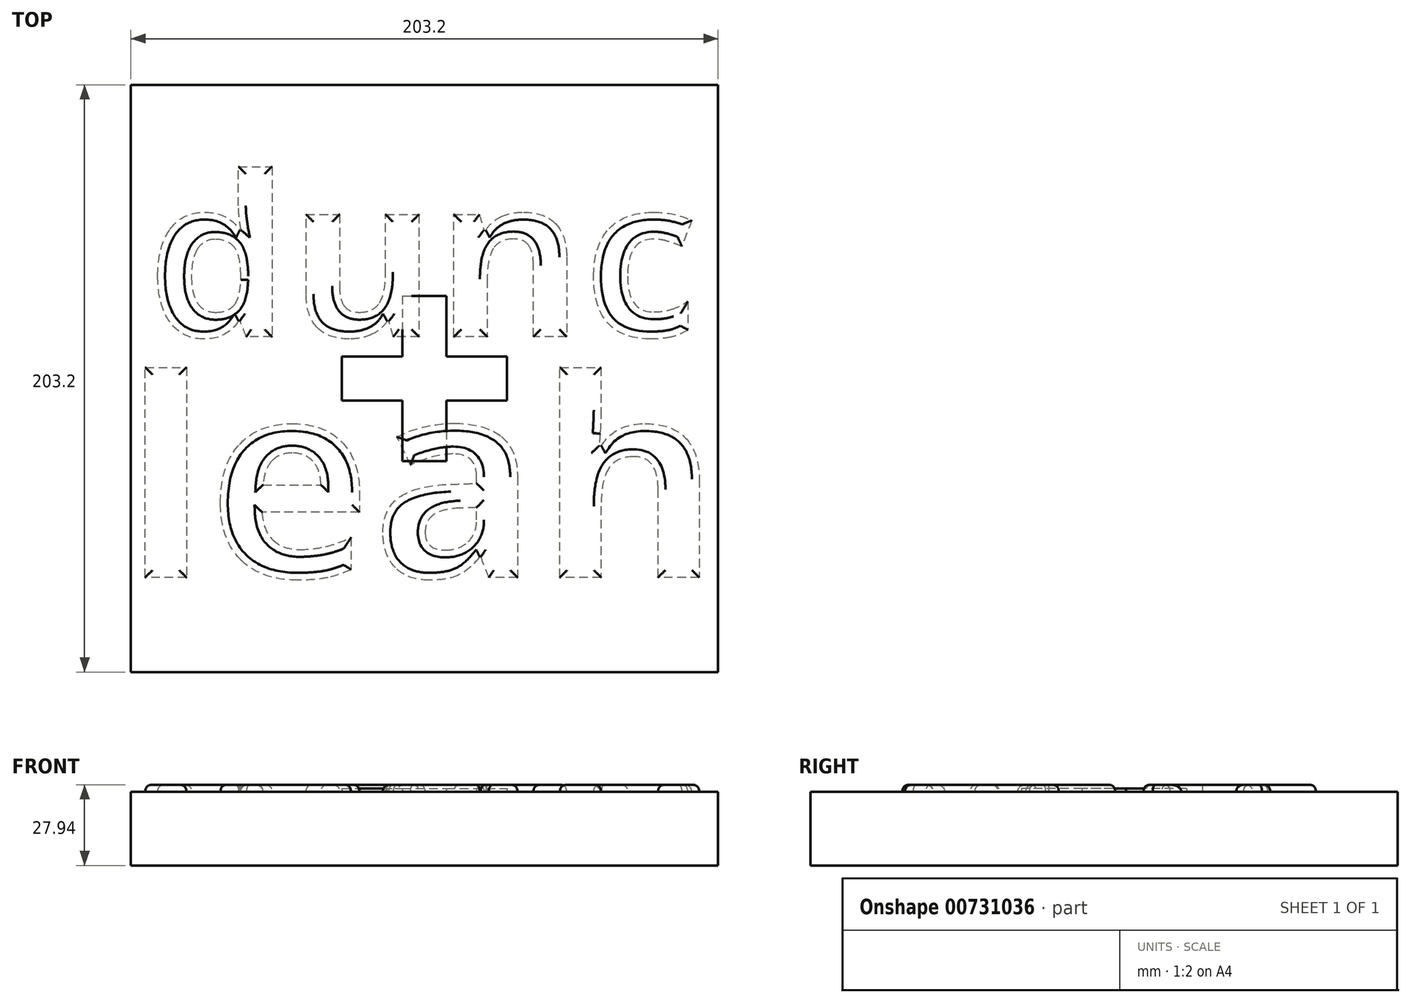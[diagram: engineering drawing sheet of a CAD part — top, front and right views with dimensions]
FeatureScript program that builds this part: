
annotation { "Feature Type Name" : "Feature", "Feature Type Description" : "" }
export const myFeature = defineFeature(function(context is Context, id is Id, definition is map)
    precondition{}
    {
        {
            var Q0;
            Q0=qCreatedBy(makeId("Top.planeOp"),FACE);
            var sketch = newSketch(context, id + "F0", { "sketchPlane" : qUnion([Q0])});
            skLineSegment(sketch, "E0.bottom", {"start": v(-101.6, 101.6) * mm, "end": v(101.6, 101.6) * mm});
            skLineSegment(sketch, "E0.top", {"start": v(-101.6, -101.6) * mm, "end": v(101.6, -101.6) * mm});
            skLineSegment(sketch, "E0.left", {"start": v(-101.6, 101.6) * mm, "end": v(-101.6, -101.6) * mm});
            skLineSegment(sketch, "E0.right", {"start": v(101.6, 101.6) * mm, "end": v(101.6, -101.6) * mm});
            skPoint(sketch, "E0.middle", {"position": v(0, 0) * mm});
            skText(sketch, "E1", { "text": "dunc", "fontName": "OpenSans-Bold.ttf"});
            skText(sketch, "E2", { "text": "leah", "fontName": "OpenSans-Bold.ttf"});
            const initialGuessF0  = {"E1": [-0.0958, 0.01441, 1, 0, 0.05578], "E2": [-0.1041, -0.06888, 1, 0, 0.06888]};
            skSetInitialGuess(sketch, initialGuessF0);
            skSolve(sketch);
        }
        {
            var Q0;
            Q0=makeQuery(id+"F0.imprint","IMPRINT",FACE,{"disambiguationData":[TD([[makeQuery(id+"F0.imprint","IMPRINT",EDGE,{"derivedFrom":sQuery(id+"F0.wireOp",EDGE,"E2.sketch_text.stroke-42")}),1.0]])]});
            var Q1;
            Q1=makeQuery(id+"F0.imprint","IMPRINT",FACE,{"disambiguationData":[TD([[makeQuery(id+"F0.imprint","IMPRINT",EDGE,{"derivedFrom":sQuery(id+"F0.wireOp",EDGE,"E1.sketch_text.stroke-14")}),1.0]])]});
            var Q2;
            Q2=makeQuery(id+"F0.imprint","IMPRINT",FACE,{"disambiguationData":[TD([[makeQuery(id+"F0.imprint","IMPRINT",EDGE,{"derivedFrom":sQuery(id+"F0.wireOp",EDGE,"E2.sketch_text.stroke-4")}),1.0]])]});
            var Q3;
            Q3=makeQuery(id+"F0.imprint","IMPRINT",FACE,{"disambiguationData":[TD([[makeQuery(id+"F0.imprint","IMPRINT",EDGE,{"derivedFrom":sQuery(id+"F0.wireOp",EDGE,"E0.bottom")}),-1.0]])]});
            var Q4;
            Q4=makeQuery(id+"F2.opExtrude","CAP_FACE",FACE,{"disambiguationData":[OSD([sQuery(id+"F0.wireOp",EDGE,"E1.sketch_text.stroke-0"),sQuery(id+"F0.wireOp",EDGE,"E1.sketch_text.stroke-1"),sQuery(id+"F0.wireOp",EDGE,"E1.sketch_text.stroke-2"),sQuery(id+"F0.wireOp",EDGE,"E1.sketch_text.stroke-3"),sQuery(id+"F0.wireOp",EDGE,"E1.sketch_text.stroke-4"),sQuery(id+"F0.wireOp",EDGE,"E1.sketch_text.stroke-5"),sQuery(id+"F0.wireOp",EDGE,"E1.sketch_text.stroke-6"),sQuery(id+"F0.wireOp",EDGE,"E1.sketch_text.stroke-7"),sQuery(id+"F0.wireOp",EDGE,"E1.sketch_text.stroke-8"),sQuery(id+"F0.wireOp",EDGE,"E1.sketch_text.stroke-9"),sQuery(id+"F0.wireOp",EDGE,"E1.sketch_text.stroke-10"),sQuery(id+"F0.wireOp",EDGE,"E1.sketch_text.stroke-11"),sQuery(id+"F0.wireOp",EDGE,"E1.sketch_text.stroke-12"),sQuery(id+"F0.wireOp",EDGE,"E1.sketch_text.stroke-13"),sQuery(id+"F0.wireOp",EDGE,"E1.sketch_text.stroke-14"),sQuery(id+"F0.wireOp",EDGE,"E1.sketch_text.stroke-15"),sQuery(id+"F0.wireOp",EDGE,"E1.sketch_text.stroke-16"),sQuery(id+"F0.wireOp",EDGE,"E1.sketch_text.stroke-17"),sQuery(id+"F0.wireOp",EDGE,"E1.sketch_text.stroke-18"),sQuery(id+"F0.wireOp",EDGE,"E1.sketch_text.stroke-19"),sQuery(id+"F0.wireOp",EDGE,"E1.sketch_text.stroke-20"),sQuery(id+"F0.wireOp",EDGE,"E1.sketch_text.stroke-21"),sQuery(id+"F0.wireOp",EDGE,"E1.sketch_text.stroke-22")])],"isStart":false});
            var Q5;
            Q5=makeQuery(id+"F2.opExtrude","CAP_FACE",FACE,{"disambiguationData":[OSD([sQuery(id+"F0.wireOp",EDGE,"E1.sketch_text.stroke-23"),sQuery(id+"F0.wireOp",EDGE,"E1.sketch_text.stroke-24"),sQuery(id+"F0.wireOp",EDGE,"E1.sketch_text.stroke-25"),sQuery(id+"F0.wireOp",EDGE,"E1.sketch_text.stroke-26"),sQuery(id+"F0.wireOp",EDGE,"E1.sketch_text.stroke-27"),sQuery(id+"F0.wireOp",EDGE,"E1.sketch_text.stroke-28"),sQuery(id+"F0.wireOp",EDGE,"E1.sketch_text.stroke-29"),sQuery(id+"F0.wireOp",EDGE,"E1.sketch_text.stroke-30"),sQuery(id+"F0.wireOp",EDGE,"E1.sketch_text.stroke-31"),sQuery(id+"F0.wireOp",EDGE,"E1.sketch_text.stroke-32"),sQuery(id+"F0.wireOp",EDGE,"E1.sketch_text.stroke-33"),sQuery(id+"F0.wireOp",EDGE,"E1.sketch_text.stroke-34"),sQuery(id+"F0.wireOp",EDGE,"E1.sketch_text.stroke-35"),sQuery(id+"F0.wireOp",EDGE,"E1.sketch_text.stroke-36"),sQuery(id+"F0.wireOp",EDGE,"E1.sketch_text.stroke-37"),sQuery(id+"F0.wireOp",EDGE,"E1.sketch_text.stroke-38"),sQuery(id+"F0.wireOp",EDGE,"E1.sketch_text.stroke-39")])],"isStart":false});
            var Q6;
            Q6=makeQuery(id+"F2.opExtrude","CAP_FACE",FACE,{"disambiguationData":[OSD([sQuery(id+"F0.wireOp",EDGE,"E1.sketch_text.stroke-40"),sQuery(id+"F0.wireOp",EDGE,"E1.sketch_text.stroke-41"),sQuery(id+"F0.wireOp",EDGE,"E1.sketch_text.stroke-42"),sQuery(id+"F0.wireOp",EDGE,"E1.sketch_text.stroke-43"),sQuery(id+"F0.wireOp",EDGE,"E1.sketch_text.stroke-44"),sQuery(id+"F0.wireOp",EDGE,"E1.sketch_text.stroke-45"),sQuery(id+"F0.wireOp",EDGE,"E1.sketch_text.stroke-46"),sQuery(id+"F0.wireOp",EDGE,"E1.sketch_text.stroke-47"),sQuery(id+"F0.wireOp",EDGE,"E1.sketch_text.stroke-48"),sQuery(id+"F0.wireOp",EDGE,"E1.sketch_text.stroke-49"),sQuery(id+"F0.wireOp",EDGE,"E1.sketch_text.stroke-50"),sQuery(id+"F0.wireOp",EDGE,"E1.sketch_text.stroke-51"),sQuery(id+"F0.wireOp",EDGE,"E1.sketch_text.stroke-52"),sQuery(id+"F0.wireOp",EDGE,"E1.sketch_text.stroke-53"),sQuery(id+"F0.wireOp",EDGE,"E1.sketch_text.stroke-54"),sQuery(id+"F0.wireOp",EDGE,"E1.sketch_text.stroke-55"),sQuery(id+"F0.wireOp",EDGE,"E1.sketch_text.stroke-56")])],"isStart":false});
            var Q7;
            Q7=makeQuery(id+"F2.opExtrude","CAP_FACE",FACE,{"disambiguationData":[OSD([sQuery(id+"F0.wireOp",EDGE,"E1.sketch_text.stroke-57"),sQuery(id+"F0.wireOp",EDGE,"E1.sketch_text.stroke-58"),sQuery(id+"F0.wireOp",EDGE,"E1.sketch_text.stroke-59"),sQuery(id+"F0.wireOp",EDGE,"E1.sketch_text.stroke-60"),sQuery(id+"F0.wireOp",EDGE,"E1.sketch_text.stroke-61"),sQuery(id+"F0.wireOp",EDGE,"E1.sketch_text.stroke-62"),sQuery(id+"F0.wireOp",EDGE,"E1.sketch_text.stroke-63"),sQuery(id+"F0.wireOp",EDGE,"E1.sketch_text.stroke-64"),sQuery(id+"F0.wireOp",EDGE,"E1.sketch_text.stroke-65"),sQuery(id+"F0.wireOp",EDGE,"E1.sketch_text.stroke-66"),sQuery(id+"F0.wireOp",EDGE,"E1.sketch_text.stroke-67"),sQuery(id+"F0.wireOp",EDGE,"E1.sketch_text.stroke-68"),sQuery(id+"F0.wireOp",EDGE,"E1.sketch_text.stroke-69"),sQuery(id+"F0.wireOp",EDGE,"E1.sketch_text.stroke-70")])],"isStart":false});
            var Q8;
            Q8=makeQuery(id+"F2.opExtrude","CAP_FACE",FACE,{"disambiguationData":[OSD([sQuery(id+"F0.wireOp",EDGE,"E2.sketch_text.stroke-49"),sQuery(id+"F0.wireOp",EDGE,"E2.sketch_text.stroke-50"),sQuery(id+"F0.wireOp",EDGE,"E2.sketch_text.stroke-51"),sQuery(id+"F0.wireOp",EDGE,"E2.sketch_text.stroke-52"),sQuery(id+"F0.wireOp",EDGE,"E2.sketch_text.stroke-53"),sQuery(id+"F0.wireOp",EDGE,"E2.sketch_text.stroke-54"),sQuery(id+"F0.wireOp",EDGE,"E2.sketch_text.stroke-55"),sQuery(id+"F0.wireOp",EDGE,"E2.sketch_text.stroke-56"),sQuery(id+"F0.wireOp",EDGE,"E2.sketch_text.stroke-57"),sQuery(id+"F0.wireOp",EDGE,"E2.sketch_text.stroke-58"),sQuery(id+"F0.wireOp",EDGE,"E2.sketch_text.stroke-59"),sQuery(id+"F0.wireOp",EDGE,"E2.sketch_text.stroke-60"),sQuery(id+"F0.wireOp",EDGE,"E2.sketch_text.stroke-61"),sQuery(id+"F0.wireOp",EDGE,"E2.sketch_text.stroke-62"),sQuery(id+"F0.wireOp",EDGE,"E2.sketch_text.stroke-63"),sQuery(id+"F0.wireOp",EDGE,"E2.sketch_text.stroke-64"),sQuery(id+"F0.wireOp",EDGE,"E2.sketch_text.stroke-65")])],"isStart":false});
            var Q9;
            Q9=makeQuery(id+"F2.opExtrude","CAP_FACE",FACE,{"disambiguationData":[OSD([sQuery(id+"F0.wireOp",EDGE,"E2.sketch_text.stroke-24"),sQuery(id+"F0.wireOp",EDGE,"E2.sketch_text.stroke-25"),sQuery(id+"F0.wireOp",EDGE,"E2.sketch_text.stroke-26"),sQuery(id+"F0.wireOp",EDGE,"E2.sketch_text.stroke-27"),sQuery(id+"F0.wireOp",EDGE,"E2.sketch_text.stroke-28"),sQuery(id+"F0.wireOp",EDGE,"E2.sketch_text.stroke-29"),sQuery(id+"F0.wireOp",EDGE,"E2.sketch_text.stroke-30"),sQuery(id+"F0.wireOp",EDGE,"E2.sketch_text.stroke-31"),sQuery(id+"F0.wireOp",EDGE,"E2.sketch_text.stroke-32"),sQuery(id+"F0.wireOp",EDGE,"E2.sketch_text.stroke-33"),sQuery(id+"F0.wireOp",EDGE,"E2.sketch_text.stroke-34"),sQuery(id+"F0.wireOp",EDGE,"E2.sketch_text.stroke-35"),sQuery(id+"F0.wireOp",EDGE,"E2.sketch_text.stroke-36"),sQuery(id+"F0.wireOp",EDGE,"E2.sketch_text.stroke-37"),sQuery(id+"F0.wireOp",EDGE,"E2.sketch_text.stroke-38"),sQuery(id+"F0.wireOp",EDGE,"E2.sketch_text.stroke-39"),sQuery(id+"F0.wireOp",EDGE,"E2.sketch_text.stroke-40"),sQuery(id+"F0.wireOp",EDGE,"E2.sketch_text.stroke-41"),sQuery(id+"F0.wireOp",EDGE,"E2.sketch_text.stroke-42"),sQuery(id+"F0.wireOp",EDGE,"E2.sketch_text.stroke-43"),sQuery(id+"F0.wireOp",EDGE,"E2.sketch_text.stroke-44"),sQuery(id+"F0.wireOp",EDGE,"E2.sketch_text.stroke-45"),sQuery(id+"F0.wireOp",EDGE,"E2.sketch_text.stroke-46"),sQuery(id+"F0.wireOp",EDGE,"E2.sketch_text.stroke-47"),sQuery(id+"F0.wireOp",EDGE,"E2.sketch_text.stroke-48")])],"isStart":false});
            var Q10;
            Q10=makeQuery(id+"F2.opExtrude","CAP_FACE",FACE,{"disambiguationData":[OSD([sQuery(id+"F0.wireOp",EDGE,"E2.sketch_text.stroke-4"),sQuery(id+"F0.wireOp",EDGE,"E2.sketch_text.stroke-5"),sQuery(id+"F0.wireOp",EDGE,"E2.sketch_text.stroke-6"),sQuery(id+"F0.wireOp",EDGE,"E2.sketch_text.stroke-7"),sQuery(id+"F0.wireOp",EDGE,"E2.sketch_text.stroke-8"),sQuery(id+"F0.wireOp",EDGE,"E2.sketch_text.stroke-9"),sQuery(id+"F0.wireOp",EDGE,"E2.sketch_text.stroke-10"),sQuery(id+"F0.wireOp",EDGE,"E2.sketch_text.stroke-11"),sQuery(id+"F0.wireOp",EDGE,"E2.sketch_text.stroke-12"),sQuery(id+"F0.wireOp",EDGE,"E2.sketch_text.stroke-13"),sQuery(id+"F0.wireOp",EDGE,"E2.sketch_text.stroke-14"),sQuery(id+"F0.wireOp",EDGE,"E2.sketch_text.stroke-15"),sQuery(id+"F0.wireOp",EDGE,"E2.sketch_text.stroke-16"),sQuery(id+"F0.wireOp",EDGE,"E2.sketch_text.stroke-17"),sQuery(id+"F0.wireOp",EDGE,"E2.sketch_text.stroke-18"),sQuery(id+"F0.wireOp",EDGE,"E2.sketch_text.stroke-19"),sQuery(id+"F0.wireOp",EDGE,"E2.sketch_text.stroke-20"),sQuery(id+"F0.wireOp",EDGE,"E2.sketch_text.stroke-21"),sQuery(id+"F0.wireOp",EDGE,"E2.sketch_text.stroke-22"),sQuery(id+"F0.wireOp",EDGE,"E2.sketch_text.stroke-23")])],"isStart":false});
            var Q11;
            Q11=makeQuery(id+"F2.opExtrude","CAP_FACE",FACE,{"disambiguationData":[OSD([sQuery(id+"F0.wireOp",EDGE,"E2.sketch_text.stroke-0"),sQuery(id+"F0.wireOp",EDGE,"E2.sketch_text.stroke-1"),sQuery(id+"F0.wireOp",EDGE,"E2.sketch_text.stroke-2"),sQuery(id+"F0.wireOp",EDGE,"E2.sketch_text.stroke-3")])],"isStart":false});
            var Q12;
            Q12=makeQuery(id+"F0.imprint","IMPRINT",FACE,{"disambiguationData":[TD([[makeQuery(id+"F0.imprint","IMPRINT",EDGE,{"derivedFrom":sQuery(id+"F0.wireOp",EDGE,"E2.sketch_text.stroke-0")}),-1.0]])]});
            var Q13;
            Q13=makeQuery(id+"F0.imprint","IMPRINT",FACE,{"disambiguationData":[TD([[makeQuery(id+"F0.imprint","IMPRINT",EDGE,{"derivedFrom":sQuery(id+"F0.wireOp",EDGE,"E2.sketch_text.stroke-4")}),-1.0]])]});
            var Q14;
            Q14=makeQuery(id+"F0.imprint","IMPRINT",FACE,{"disambiguationData":[TD([[makeQuery(id+"F0.imprint","IMPRINT",EDGE,{"derivedFrom":sQuery(id+"F0.wireOp",EDGE,"E2.sketch_text.stroke-24")}),-1.0]])]});
            var Q15;
            Q15=makeQuery(id+"F0.imprint","IMPRINT",FACE,{"disambiguationData":[TD([[makeQuery(id+"F0.imprint","IMPRINT",EDGE,{"derivedFrom":sQuery(id+"F0.wireOp",EDGE,"E2.sketch_text.stroke-49")}),-1.0]])]});
            var Q16;
            Q16=makeQuery(id+"F0.imprint","IMPRINT",FACE,{"disambiguationData":[TD([[makeQuery(id+"F0.imprint","IMPRINT",EDGE,{"derivedFrom":sQuery(id+"F0.wireOp",EDGE,"E1.sketch_text.stroke-57")}),-1.0]])]});
            var Q17;
            Q17=makeQuery(id+"F0.imprint","IMPRINT",FACE,{"disambiguationData":[TD([[makeQuery(id+"F0.imprint","IMPRINT",EDGE,{"derivedFrom":sQuery(id+"F0.wireOp",EDGE,"E1.sketch_text.stroke-40")}),-1.0]])]});
            var Q18;
            Q18=makeQuery(id+"F0.imprint","IMPRINT",FACE,{"disambiguationData":[TD([[makeQuery(id+"F0.imprint","IMPRINT",EDGE,{"derivedFrom":sQuery(id+"F0.wireOp",EDGE,"E1.sketch_text.stroke-23")}),-1.0]])]});
            var Q19;
            Q19=makeQuery(id+"F0.imprint","IMPRINT",FACE,{"disambiguationData":[TD([[makeQuery(id+"F0.imprint","IMPRINT",EDGE,{"derivedFrom":sQuery(id+"F0.wireOp",EDGE,"E1.sketch_text.stroke-0")}),-1.0]])]});
            extrude(context, id + "F1", {"entities" : qUnion([Q0, Q1, Q2, Q3, Q4, Q5, Q6, Q7, Q8, Q9, Q10, Q11, Q12, Q13, Q14, Q15, Q16, Q17, Q18, Q19]), "oppositeDirection" : true, "depth" : 25.4 * mm, "offsetDistance" : 25.4 * mm, "hasSecondDirection" : true, "secondDirectionOppositeDirection" : false, "secondDirectionDepth" : 0.03 * mm});
        }
        {
            var Q0;
            Q0=makeQuery(id+"F0.imprint","IMPRINT",FACE,{"disambiguationData":[TD([[makeQuery(id+"F0.imprint","IMPRINT",EDGE,{"derivedFrom":sQuery(id+"F0.wireOp",EDGE,"E1.sketch_text.stroke-0")}),-1.0]])]});
            var Q1;
            Q1=makeQuery(id+"F0.imprint","IMPRINT",FACE,{"disambiguationData":[TD([[makeQuery(id+"F0.imprint","IMPRINT",EDGE,{"derivedFrom":sQuery(id+"F0.wireOp",EDGE,"E1.sketch_text.stroke-23")}),-1.0]])]});
            var Q2;
            Q2=makeQuery(id+"F0.imprint","IMPRINT",FACE,{"disambiguationData":[TD([[makeQuery(id+"F0.imprint","IMPRINT",EDGE,{"derivedFrom":sQuery(id+"F0.wireOp",EDGE,"E1.sketch_text.stroke-40")}),-1.0]])]});
            var Q3;
            Q3=makeQuery(id+"F0.imprint","IMPRINT",FACE,{"disambiguationData":[TD([[makeQuery(id+"F0.imprint","IMPRINT",EDGE,{"derivedFrom":sQuery(id+"F0.wireOp",EDGE,"E1.sketch_text.stroke-57")}),-1.0]])]});
            var Q4;
            Q4=makeQuery(id+"F0.imprint","IMPRINT",FACE,{"disambiguationData":[TD([[makeQuery(id+"F0.imprint","IMPRINT",EDGE,{"derivedFrom":sQuery(id+"F0.wireOp",EDGE,"E2.sketch_text.stroke-49")}),-1.0]])]});
            var Q5;
            Q5=makeQuery(id+"F0.imprint","IMPRINT",FACE,{"disambiguationData":[TD([[makeQuery(id+"F0.imprint","IMPRINT",EDGE,{"derivedFrom":sQuery(id+"F0.wireOp",EDGE,"E2.sketch_text.stroke-24")}),-1.0]])]});
            var Q6;
            Q6=makeQuery(id+"F0.imprint","IMPRINT",FACE,{"disambiguationData":[TD([[makeQuery(id+"F0.imprint","IMPRINT",EDGE,{"derivedFrom":sQuery(id+"F0.wireOp",EDGE,"E2.sketch_text.stroke-4")}),-1.0]])]});
            var Q7;
            Q7=makeQuery(id+"F0.imprint","IMPRINT",FACE,{"disambiguationData":[TD([[makeQuery(id+"F0.imprint","IMPRINT",EDGE,{"derivedFrom":sQuery(id+"F0.wireOp",EDGE,"E2.sketch_text.stroke-0")}),-1.0]])]});
            extrude(context, id + "F2", {"entities" : qUnion([Q0, Q1, Q2, Q3, Q4, Q5, Q6, Q7]), "depth" : 2.54 * mm, "offsetDistance" : 25.4 * mm});
        }
        {
            var Q0;
            Q0=qCreatedBy(makeId("Top.planeOp"),FACE);
            var sketch = newSketch(context, id + "F3", { "sketchPlane" : qUnion([Q0])});
            skLineSegment(sketch, "E3.bottom", {"start": v(-7.62, 28.58) * mm, "end": v(7.62, 28.58) * mm});
            skLineSegment(sketch, "E3.top", {"start": v(-7.62, -28.58) * mm, "end": v(7.62, -28.58) * mm});
            skLineSegment(sketch, "E3.left", {"start": v(-7.62, 28.58) * mm, "end": v(-7.62, 7.62) * mm});
            skLineSegment(sketch, "E3.right", {"start": v(7.62, 28.58) * mm, "end": v(7.62, 8.04) * mm});
            skPoint(sketch, "E3.middle", {"position": v(0, 0) * mm});
            skLineSegment(sketch, "E4.bottom", {"start": v(-28.58, 7.62) * mm, "end": v(-7.62, 7.62) * mm});
            skLineSegment(sketch, "E4.top", {"start": v(-28.58, -7.62) * mm, "end": v(-7.62, -7.62) * mm});
            skLineSegment(sketch, "E4.left", {"start": v(-28.57, 7.62) * mm, "end": v(-28.58, -7.62) * mm});
            skLineSegment(sketch, "E4.right", {"start": v(28.58, 7.62) * mm, "end": v(28.58, -7.62) * mm});
            skLineSegment(sketch, "E5", {"start": v(7.62, 8.04) * mm, "end": v(7.62, 7.62) * mm});
            skLineSegment(sketch, "E6", {"start": v(7.62, -7.62) * mm, "end": v(7.62, -28.58) * mm});
            skLineSegment(sketch, "E7", {"start": v(7.62, -7.62) * mm, "end": v(28.58, -7.62) * mm});
            skLineSegment(sketch, "E8", {"start": v(-7.62, -7.62) * mm, "end": v(-7.62, -28.58) * mm});
            skLineSegment(sketch, "E9.trimOffspring", {"start": v(7.62, 7.62) * mm, "end": v(28.58, 7.62) * mm});
            skSolve(sketch);
        }
        {
            var Q0;
            Q0=makeQuery(id+"F3.imprint","IMPRINT",FACE,{"disambiguationData":[TD([[makeQuery(id+"F3.imprint","IMPRINT",EDGE,{"derivedFrom":sQuery(id+"F3.wireOp",EDGE,"E3.bottom")}),-1.0]])]});
            extrude(context, id + "F4", {"entities" : qUnion([Q0]), "depth" : 1.27 * mm, "offsetDistance" : 25.4 * mm});
        }
        {
            var Q0;
            Q0=makeQuery(id+"F2.opExtrude","CAP_FACE",FACE,{"disambiguationData":[OSD([sQuery(id+"F0.wireOp",EDGE,"E1.sketch_text.stroke-23"),sQuery(id+"F0.wireOp",EDGE,"E1.sketch_text.stroke-24"),sQuery(id+"F0.wireOp",EDGE,"E1.sketch_text.stroke-25"),sQuery(id+"F0.wireOp",EDGE,"E1.sketch_text.stroke-26"),sQuery(id+"F0.wireOp",EDGE,"E1.sketch_text.stroke-27"),sQuery(id+"F0.wireOp",EDGE,"E1.sketch_text.stroke-28"),sQuery(id+"F0.wireOp",EDGE,"E1.sketch_text.stroke-29"),sQuery(id+"F0.wireOp",EDGE,"E1.sketch_text.stroke-30"),sQuery(id+"F0.wireOp",EDGE,"E1.sketch_text.stroke-31"),sQuery(id+"F0.wireOp",EDGE,"E1.sketch_text.stroke-32"),sQuery(id+"F0.wireOp",EDGE,"E1.sketch_text.stroke-33"),sQuery(id+"F0.wireOp",EDGE,"E1.sketch_text.stroke-34"),sQuery(id+"F0.wireOp",EDGE,"E1.sketch_text.stroke-35"),sQuery(id+"F0.wireOp",EDGE,"E1.sketch_text.stroke-36"),sQuery(id+"F0.wireOp",EDGE,"E1.sketch_text.stroke-37"),sQuery(id+"F0.wireOp",EDGE,"E1.sketch_text.stroke-38"),sQuery(id+"F0.wireOp",EDGE,"E1.sketch_text.stroke-39")])],"isStart":false});
            var Q1;
            Q1=makeQuery(id+"F2.opExtrude","CAP_FACE",FACE,{"disambiguationData":[OSD([sQuery(id+"F0.wireOp",EDGE,"E1.sketch_text.stroke-0"),sQuery(id+"F0.wireOp",EDGE,"E1.sketch_text.stroke-1"),sQuery(id+"F0.wireOp",EDGE,"E1.sketch_text.stroke-2"),sQuery(id+"F0.wireOp",EDGE,"E1.sketch_text.stroke-3"),sQuery(id+"F0.wireOp",EDGE,"E1.sketch_text.stroke-4"),sQuery(id+"F0.wireOp",EDGE,"E1.sketch_text.stroke-5"),sQuery(id+"F0.wireOp",EDGE,"E1.sketch_text.stroke-6"),sQuery(id+"F0.wireOp",EDGE,"E1.sketch_text.stroke-7"),sQuery(id+"F0.wireOp",EDGE,"E1.sketch_text.stroke-8"),sQuery(id+"F0.wireOp",EDGE,"E1.sketch_text.stroke-9"),sQuery(id+"F0.wireOp",EDGE,"E1.sketch_text.stroke-10"),sQuery(id+"F0.wireOp",EDGE,"E1.sketch_text.stroke-11"),sQuery(id+"F0.wireOp",EDGE,"E1.sketch_text.stroke-12"),sQuery(id+"F0.wireOp",EDGE,"E1.sketch_text.stroke-13"),sQuery(id+"F0.wireOp",EDGE,"E1.sketch_text.stroke-14"),sQuery(id+"F0.wireOp",EDGE,"E1.sketch_text.stroke-15"),sQuery(id+"F0.wireOp",EDGE,"E1.sketch_text.stroke-16"),sQuery(id+"F0.wireOp",EDGE,"E1.sketch_text.stroke-17"),sQuery(id+"F0.wireOp",EDGE,"E1.sketch_text.stroke-18"),sQuery(id+"F0.wireOp",EDGE,"E1.sketch_text.stroke-19"),sQuery(id+"F0.wireOp",EDGE,"E1.sketch_text.stroke-20"),sQuery(id+"F0.wireOp",EDGE,"E1.sketch_text.stroke-21"),sQuery(id+"F0.wireOp",EDGE,"E1.sketch_text.stroke-22")])],"isStart":false});
            var Q2;
            Q2=makeQuery(id+"F2.opExtrude","CAP_FACE",FACE,{"disambiguationData":[OSD([sQuery(id+"F0.wireOp",EDGE,"E1.sketch_text.stroke-40"),sQuery(id+"F0.wireOp",EDGE,"E1.sketch_text.stroke-41"),sQuery(id+"F0.wireOp",EDGE,"E1.sketch_text.stroke-42"),sQuery(id+"F0.wireOp",EDGE,"E1.sketch_text.stroke-43"),sQuery(id+"F0.wireOp",EDGE,"E1.sketch_text.stroke-44"),sQuery(id+"F0.wireOp",EDGE,"E1.sketch_text.stroke-45"),sQuery(id+"F0.wireOp",EDGE,"E1.sketch_text.stroke-46"),sQuery(id+"F0.wireOp",EDGE,"E1.sketch_text.stroke-47"),sQuery(id+"F0.wireOp",EDGE,"E1.sketch_text.stroke-48"),sQuery(id+"F0.wireOp",EDGE,"E1.sketch_text.stroke-49"),sQuery(id+"F0.wireOp",EDGE,"E1.sketch_text.stroke-50"),sQuery(id+"F0.wireOp",EDGE,"E1.sketch_text.stroke-51"),sQuery(id+"F0.wireOp",EDGE,"E1.sketch_text.stroke-52"),sQuery(id+"F0.wireOp",EDGE,"E1.sketch_text.stroke-53"),sQuery(id+"F0.wireOp",EDGE,"E1.sketch_text.stroke-54"),sQuery(id+"F0.wireOp",EDGE,"E1.sketch_text.stroke-55"),sQuery(id+"F0.wireOp",EDGE,"E1.sketch_text.stroke-56")])],"isStart":false});
            var Q3;
            Q3=makeQuery(id+"F2.opExtrude","CAP_FACE",FACE,{"disambiguationData":[OSD([sQuery(id+"F0.wireOp",EDGE,"E1.sketch_text.stroke-57"),sQuery(id+"F0.wireOp",EDGE,"E1.sketch_text.stroke-58"),sQuery(id+"F0.wireOp",EDGE,"E1.sketch_text.stroke-59"),sQuery(id+"F0.wireOp",EDGE,"E1.sketch_text.stroke-60"),sQuery(id+"F0.wireOp",EDGE,"E1.sketch_text.stroke-61"),sQuery(id+"F0.wireOp",EDGE,"E1.sketch_text.stroke-62"),sQuery(id+"F0.wireOp",EDGE,"E1.sketch_text.stroke-63"),sQuery(id+"F0.wireOp",EDGE,"E1.sketch_text.stroke-64"),sQuery(id+"F0.wireOp",EDGE,"E1.sketch_text.stroke-65"),sQuery(id+"F0.wireOp",EDGE,"E1.sketch_text.stroke-66"),sQuery(id+"F0.wireOp",EDGE,"E1.sketch_text.stroke-67"),sQuery(id+"F0.wireOp",EDGE,"E1.sketch_text.stroke-68"),sQuery(id+"F0.wireOp",EDGE,"E1.sketch_text.stroke-69"),sQuery(id+"F0.wireOp",EDGE,"E1.sketch_text.stroke-70")])],"isStart":false});
            var Q4;
            Q4=makeQuery(id+"F2.opExtrude","CAP_FACE",FACE,{"disambiguationData":[OSD([sQuery(id+"F0.wireOp",EDGE,"E2.sketch_text.stroke-49"),sQuery(id+"F0.wireOp",EDGE,"E2.sketch_text.stroke-50"),sQuery(id+"F0.wireOp",EDGE,"E2.sketch_text.stroke-51"),sQuery(id+"F0.wireOp",EDGE,"E2.sketch_text.stroke-52"),sQuery(id+"F0.wireOp",EDGE,"E2.sketch_text.stroke-53"),sQuery(id+"F0.wireOp",EDGE,"E2.sketch_text.stroke-54"),sQuery(id+"F0.wireOp",EDGE,"E2.sketch_text.stroke-55"),sQuery(id+"F0.wireOp",EDGE,"E2.sketch_text.stroke-56"),sQuery(id+"F0.wireOp",EDGE,"E2.sketch_text.stroke-57"),sQuery(id+"F0.wireOp",EDGE,"E2.sketch_text.stroke-58"),sQuery(id+"F0.wireOp",EDGE,"E2.sketch_text.stroke-59"),sQuery(id+"F0.wireOp",EDGE,"E2.sketch_text.stroke-60"),sQuery(id+"F0.wireOp",EDGE,"E2.sketch_text.stroke-61"),sQuery(id+"F0.wireOp",EDGE,"E2.sketch_text.stroke-62"),sQuery(id+"F0.wireOp",EDGE,"E2.sketch_text.stroke-63"),sQuery(id+"F0.wireOp",EDGE,"E2.sketch_text.stroke-64"),sQuery(id+"F0.wireOp",EDGE,"E2.sketch_text.stroke-65")])],"isStart":false});
            var Q5;
            Q5=makeQuery(id+"F2.opExtrude","CAP_FACE",FACE,{"disambiguationData":[OSD([sQuery(id+"F0.wireOp",EDGE,"E2.sketch_text.stroke-0"),sQuery(id+"F0.wireOp",EDGE,"E2.sketch_text.stroke-1"),sQuery(id+"F0.wireOp",EDGE,"E2.sketch_text.stroke-2"),sQuery(id+"F0.wireOp",EDGE,"E2.sketch_text.stroke-3")])],"isStart":false});
            var Q6;
            Q6=makeQuery(id+"F2.opExtrude","CAP_FACE",FACE,{"disambiguationData":[OSD([sQuery(id+"F0.wireOp",EDGE,"E2.sketch_text.stroke-24"),sQuery(id+"F0.wireOp",EDGE,"E2.sketch_text.stroke-25"),sQuery(id+"F0.wireOp",EDGE,"E2.sketch_text.stroke-26"),sQuery(id+"F0.wireOp",EDGE,"E2.sketch_text.stroke-27"),sQuery(id+"F0.wireOp",EDGE,"E2.sketch_text.stroke-28"),sQuery(id+"F0.wireOp",EDGE,"E2.sketch_text.stroke-29"),sQuery(id+"F0.wireOp",EDGE,"E2.sketch_text.stroke-30"),sQuery(id+"F0.wireOp",EDGE,"E2.sketch_text.stroke-31"),sQuery(id+"F0.wireOp",EDGE,"E2.sketch_text.stroke-32"),sQuery(id+"F0.wireOp",EDGE,"E2.sketch_text.stroke-33"),sQuery(id+"F0.wireOp",EDGE,"E2.sketch_text.stroke-34"),sQuery(id+"F0.wireOp",EDGE,"E2.sketch_text.stroke-35"),sQuery(id+"F0.wireOp",EDGE,"E2.sketch_text.stroke-36"),sQuery(id+"F0.wireOp",EDGE,"E2.sketch_text.stroke-37"),sQuery(id+"F0.wireOp",EDGE,"E2.sketch_text.stroke-38"),sQuery(id+"F0.wireOp",EDGE,"E2.sketch_text.stroke-39"),sQuery(id+"F0.wireOp",EDGE,"E2.sketch_text.stroke-40"),sQuery(id+"F0.wireOp",EDGE,"E2.sketch_text.stroke-41"),sQuery(id+"F0.wireOp",EDGE,"E2.sketch_text.stroke-42"),sQuery(id+"F0.wireOp",EDGE,"E2.sketch_text.stroke-43"),sQuery(id+"F0.wireOp",EDGE,"E2.sketch_text.stroke-44"),sQuery(id+"F0.wireOp",EDGE,"E2.sketch_text.stroke-45"),sQuery(id+"F0.wireOp",EDGE,"E2.sketch_text.stroke-46"),sQuery(id+"F0.wireOp",EDGE,"E2.sketch_text.stroke-47"),sQuery(id+"F0.wireOp",EDGE,"E2.sketch_text.stroke-48")])],"isStart":false});
            var Q7;
            Q7=makeQuery(id+"F2.opExtrude","CAP_FACE",FACE,{"disambiguationData":[OSD([sQuery(id+"F0.wireOp",EDGE,"E2.sketch_text.stroke-4"),sQuery(id+"F0.wireOp",EDGE,"E2.sketch_text.stroke-5"),sQuery(id+"F0.wireOp",EDGE,"E2.sketch_text.stroke-6"),sQuery(id+"F0.wireOp",EDGE,"E2.sketch_text.stroke-7"),sQuery(id+"F0.wireOp",EDGE,"E2.sketch_text.stroke-8"),sQuery(id+"F0.wireOp",EDGE,"E2.sketch_text.stroke-9"),sQuery(id+"F0.wireOp",EDGE,"E2.sketch_text.stroke-10"),sQuery(id+"F0.wireOp",EDGE,"E2.sketch_text.stroke-11"),sQuery(id+"F0.wireOp",EDGE,"E2.sketch_text.stroke-12"),sQuery(id+"F0.wireOp",EDGE,"E2.sketch_text.stroke-13"),sQuery(id+"F0.wireOp",EDGE,"E2.sketch_text.stroke-14"),sQuery(id+"F0.wireOp",EDGE,"E2.sketch_text.stroke-15"),sQuery(id+"F0.wireOp",EDGE,"E2.sketch_text.stroke-16"),sQuery(id+"F0.wireOp",EDGE,"E2.sketch_text.stroke-17"),sQuery(id+"F0.wireOp",EDGE,"E2.sketch_text.stroke-18"),sQuery(id+"F0.wireOp",EDGE,"E2.sketch_text.stroke-19"),sQuery(id+"F0.wireOp",EDGE,"E2.sketch_text.stroke-20"),sQuery(id+"F0.wireOp",EDGE,"E2.sketch_text.stroke-21"),sQuery(id+"F0.wireOp",EDGE,"E2.sketch_text.stroke-22"),sQuery(id+"F0.wireOp",EDGE,"E2.sketch_text.stroke-23")])],"isStart":false});
            fillet(context, id + "F5", {"entities" : qUnion([Q0, Q1, Q2, Q3, Q4, Q5, Q6, Q7]), "radius" : 2.54 * mm, "tangentPropagation" : true, "rho" : 0.5, "crossSection" : FilletCrossSection.CONIC, "allowEdgeOverflow" : false});
        }
    });
